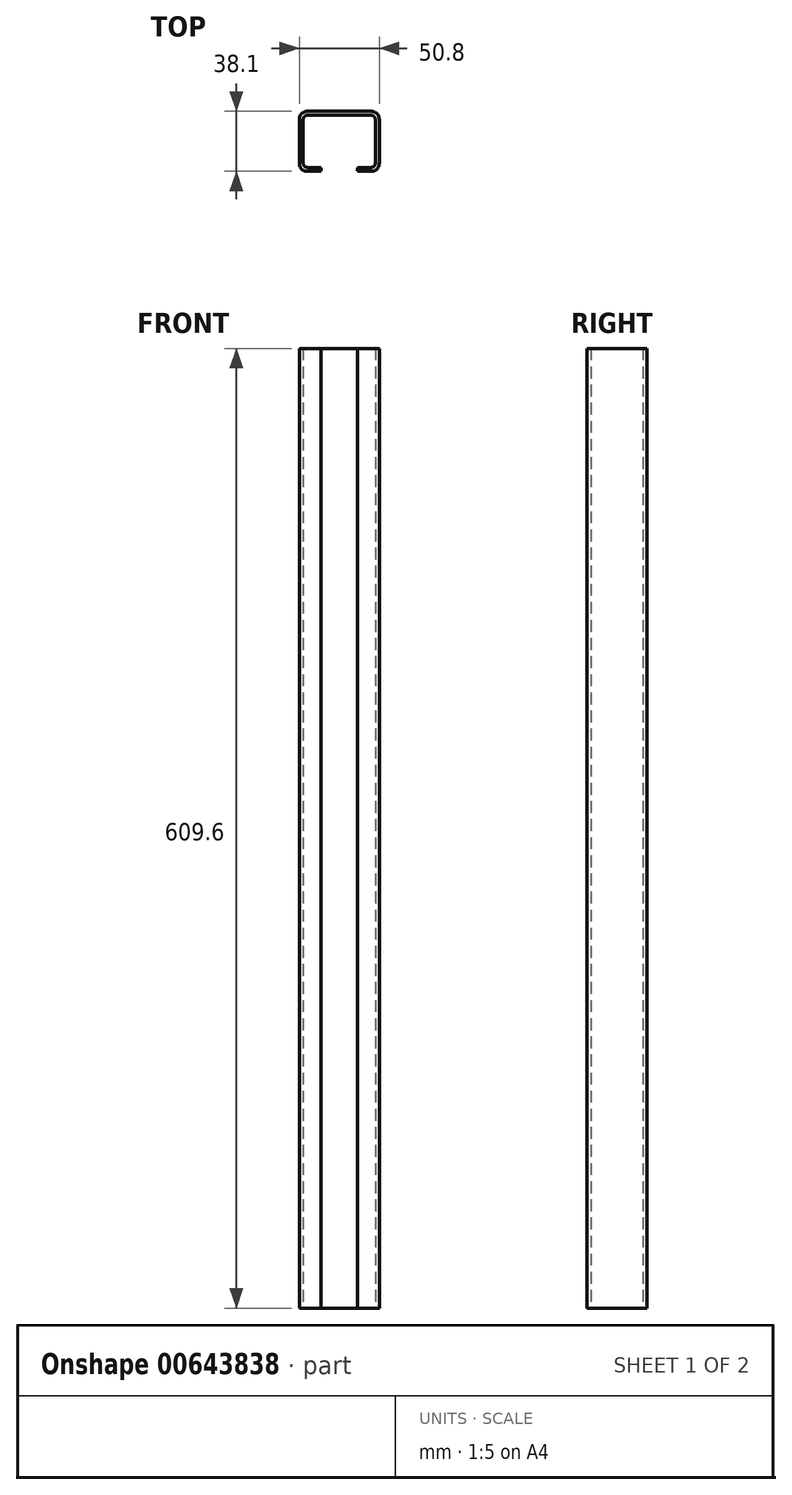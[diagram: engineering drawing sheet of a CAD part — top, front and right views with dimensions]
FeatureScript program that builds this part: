
annotation { "Feature Type Name" : "Feature", "Feature Type Description" : "" }
export const myFeature = defineFeature(function(context is Context, id is Id, definition is map)
    precondition{}
    {
        {
            var Q0;
            Q0=qCreatedBy(makeId("Top.planeOp"),FACE);
            var sketch = newSketch(context, id + "F0", { "sketchPlane" : qUnion([Q0])});
            skLineSegment(sketch, "E0", {"start": v(-11.51, -38.1) * mm, "end": v(-20.32, -38.1) * mm});
            skLineSegment(sketch, "E1", {"start": v(-25.4, -33.02) * mm, "end": v(-25.4, -5.08) * mm});
            skLineSegment(sketch, "E2", {"start": v(-20.32, 0) * mm, "end": v(20.32, 0) * mm});
            skLineSegment(sketch, "E3", {"start": v(25.4, -5.08) * mm, "end": v(25.4, -33.02) * mm});
            skLineSegment(sketch, "E4", {"start": v(20.32, -38.1) * mm, "end": v(11.51, -38.1) * mm});
            skPoint(sketch, "E5.visualSharp", {"position": v(-25.4, -38.1) * mm});
            skArc(sketch, "E5.filletArc", {"start": v(-25.4, -33.02) * mm, "mid": v(-23.91, -36.61) * mm, "end": v(-20.32, -38.1) * mm});
            skPoint(sketch, "E6.visualSharp", {"position": v(-25.4, 0) * mm});
            skArc(sketch, "E6.filletArc", {"start": v(-20.32, 0) * mm, "mid": v(-23.91, -1.49) * mm, "end": v(-25.4, -5.08) * mm});
            skPoint(sketch, "E7.visualSharp", {"position": v(25.4, 0) * mm});
            skArc(sketch, "E7.filletArc", {"start": v(25.4, -5.08) * mm, "mid": v(23.91, -1.49) * mm, "end": v(20.32, 0) * mm});
            skPoint(sketch, "E8.visualSharp", {"position": v(25.4, -38.1) * mm});
            skArc(sketch, "E8.filletArc", {"start": v(20.32, -38.1) * mm, "mid": v(23.91, -36.61) * mm, "end": v(25.4, -33.02) * mm});
            skLineSegment(sketch, "E9", {"start": v(0, 0) * mm, "end": v(0, -38.1) * mm, "construction": true});
            skLineSegment(sketch, "E10.0", {"start": v(20.32, -35.58) * mm, "end": v(11.51, -35.58) * mm});
            skArc(sketch, "E10.1", {"start": v(20.32, -35.58) * mm, "mid": v(22.13, -34.83) * mm, "end": v(22.88, -33.02) * mm});
            skLineSegment(sketch, "E10.2", {"start": v(22.88, -5.08) * mm, "end": v(22.88, -33.02) * mm});
            skArc(sketch, "E10.3", {"start": v(22.88, -5.08) * mm, "mid": v(22.13, -3.27) * mm, "end": v(20.32, -2.52) * mm});
            skLineSegment(sketch, "E10.4", {"start": v(-20.32, -2.52) * mm, "end": v(20.32, -2.52) * mm});
            skLineSegment(sketch, "E10.5", {"start": v(-11.51, -35.58) * mm, "end": v(-20.32, -35.58) * mm});
            skArc(sketch, "E10.6", {"start": v(-22.88, -33.02) * mm, "mid": v(-22.13, -34.83) * mm, "end": v(-20.32, -35.58) * mm});
            skLineSegment(sketch, "E10.7", {"start": v(-22.88, -33.02) * mm, "end": v(-22.88, -5.08) * mm});
            skArc(sketch, "E10.8", {"start": v(-20.32, -2.52) * mm, "mid": v(-22.13, -3.27) * mm, "end": v(-22.88, -5.08) * mm});
            skLineSegment(sketch, "E11", {"start": v(11.51, -35.58) * mm, "end": v(11.51, -38.1) * mm});
            skLineSegment(sketch, "E12", {"start": v(-11.51, -35.58) * mm, "end": v(-11.51, -38.1) * mm});
            skSolve(sketch);
        }
        {
            var Q0;
            Q0=makeQuery(id+"F0.imprint","IMPRINT",FACE,{"disambiguationData":[TD([[makeQuery(id+"F0.imprint","IMPRINT",EDGE,{"derivedFrom":sQuery(id+"F0.wireOp",EDGE,"E0")}),-1.0]])]});
            extrude(context, id + "F1", {"entities" : qUnion([Q0]), "depth" : 609.6 * mm, "offsetDistance" : 25.4 * mm});
        }
    });
